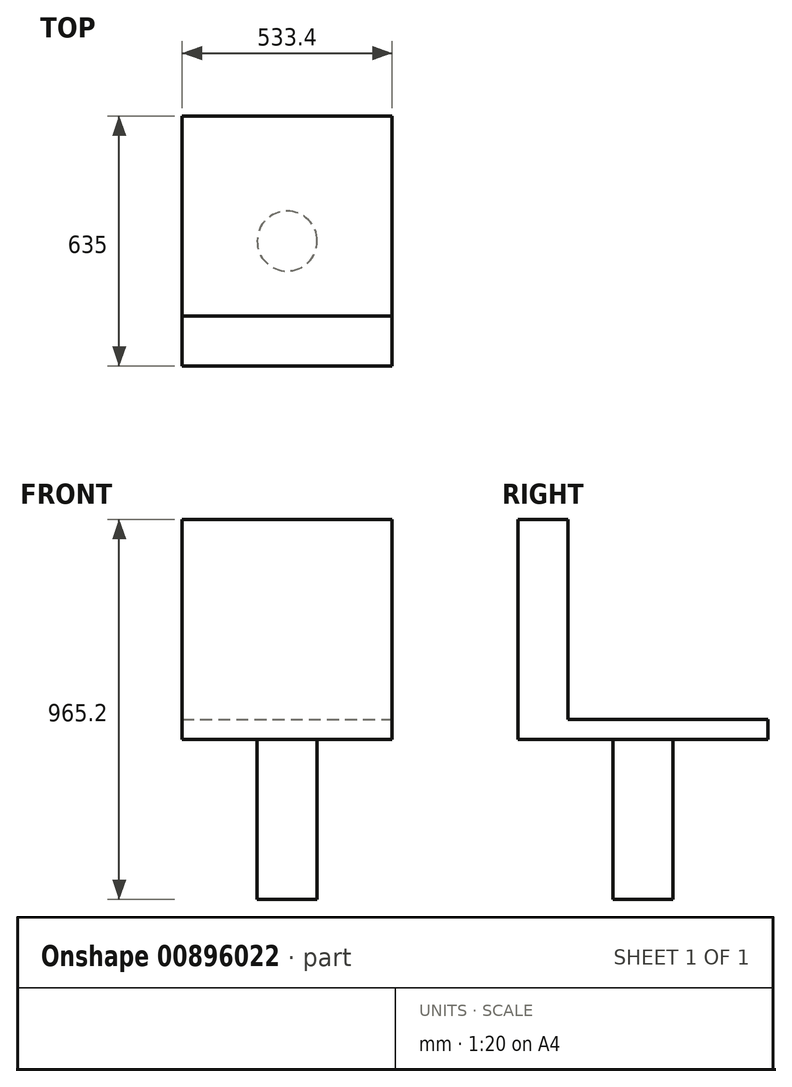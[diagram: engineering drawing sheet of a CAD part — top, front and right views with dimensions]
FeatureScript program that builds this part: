
annotation { "Feature Type Name" : "Feature", "Feature Type Description" : "" }
export const myFeature = defineFeature(function(context is Context, id is Id, definition is map)
    precondition{}
    {
        {
            var Q0;
            Q0=qCreatedBy(makeId("Top.planeOp"),FACE);
            var sketch = newSketch(context, id + "F0", { "sketchPlane" : qUnion([Q0])});
            skLineSegment(sketch, "E0.bottom", {"start": v(0, 0) * mm, "end": v(533.4, 0) * mm});
            skLineSegment(sketch, "E0.top", {"start": v(0, 635) * mm, "end": v(533.4, 635) * mm});
            skLineSegment(sketch, "E0.left", {"start": v(0, 0) * mm, "end": v(0, 635) * mm});
            skLineSegment(sketch, "E0.right", {"start": v(533.4, 0) * mm, "end": v(533.4, 635) * mm});
            skSolve(sketch);
        }
        {
            var Q0;
            Q0 = qSketchRegion(id + "F0", true);
            extrude(context, id + "F1", {"entities" : qUnion([Q0]), "depth" : 50.8 * mm, "offsetDistance" : 25.4 * mm});
        }
        {
            var Q0;
            Q0=makeQuery(id+"F1.opExtrude","CAP_FACE",FACE,{"disambiguationData":[OSD([sQuery(id+"F0.wireOp",EDGE,"E0.bottom"),sQuery(id+"F0.wireOp",EDGE,"E0.top"),sQuery(id+"F0.wireOp",EDGE,"E0.left"),sQuery(id+"F0.wireOp",EDGE,"E0.right")])],"isStart":false});
            var sketch = newSketch(context, id + "F2", { "sketchPlane" : qUnion([Q0])});
            skLineSegment(sketch, "E1.bottom", {"start": v(0, 0) * mm, "end": v(533.4, 0) * mm});
            skLineSegment(sketch, "E1.top", {"start": v(0, 127) * mm, "end": v(533.4, 127) * mm});
            skLineSegment(sketch, "E1.left", {"start": v(0, 0) * mm, "end": v(0, 127) * mm});
            skLineSegment(sketch, "E1.right", {"start": v(533.4, 0) * mm, "end": v(533.4, 127) * mm});
            skSolve(sketch);
        }
        {
            var Q0;
            Q0 = qSketchRegion(id + "F2", true);
            extrude(context, id + "F3", {"entities" : qUnion([Q0]), "operationType" : NewBodyOperationType.ADD, "depth" : 508 * mm, "offsetDistance" : 25.4 * mm});
        }
        {
            var Q0;
            Q0=makeQuery(id+"F1.opExtrude","CAP_FACE",FACE,{"disambiguationData":[OSD([sQuery(id+"F0.wireOp",EDGE,"E0.bottom"),sQuery(id+"F0.wireOp",EDGE,"E0.top"),sQuery(id+"F0.wireOp",EDGE,"E0.left"),sQuery(id+"F0.wireOp",EDGE,"E0.right")])],"isStart":true});
            var sketch = newSketch(context, id + "F4", { "sketchPlane" : qUnion([Q0])});
            skCircle(sketch, "E2", {"center": v(266.7, -317.5) * mm, "radius": 76.2 * mm});
            skLineSegment(sketch, "E3", {"start": v(533.4, 0) * mm, "end": v(0, -635) * mm, "construction": true});
            skSolve(sketch);
        }
        {
            var Q0;
            Q0 = qSketchRegion(id + "F4", true);
            extrude(context, id + "F5", {"entities" : qUnion([Q0]), "operationType" : NewBodyOperationType.ADD, "depth" : 406.4 * mm, "offsetDistance" : 25.4 * mm});
        }
    });
